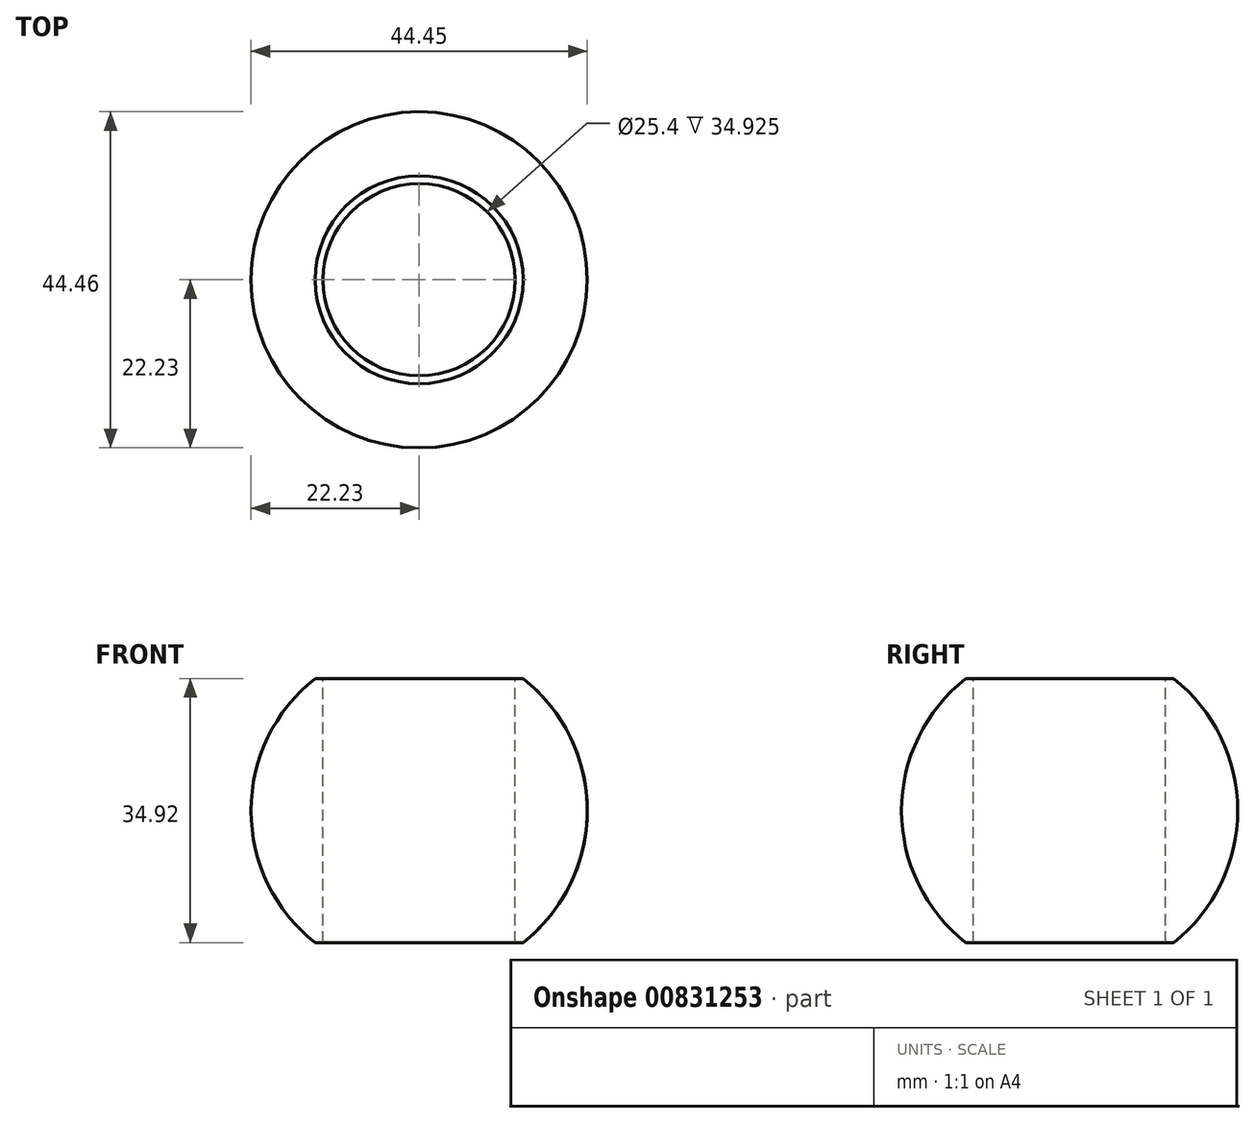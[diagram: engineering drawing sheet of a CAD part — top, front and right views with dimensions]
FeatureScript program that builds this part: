
annotation { "Feature Type Name" : "Feature", "Feature Type Description" : "" }
export const myFeature = defineFeature(function(context is Context, id is Id, definition is map)
    precondition{}
    {
        {
            var Q0;
            Q0=qCreatedBy(makeId("Front.planeOp"),FACE);
            var sketch = newSketch(context, id + "F0", { "sketchPlane" : qUnion([Q0])});
            skArc(sketch, "E0", {"start": v(-13.75, 17.46) * mm, "mid": v(-22.23, 0) * mm, "end": v(-13.75, -17.46) * mm});
            skLineSegment(sketch, "E1", {"start": v(0, 17.46) * mm, "end": v(0, -17.46) * mm, "construction": true});
            skLineSegment(sketch, "E2", {"start": v(-13.75, 17.46) * mm, "end": v(-12.7, 17.46) * mm});
            skLineSegment(sketch, "E3", {"start": v(-12.7, -17.46) * mm, "end": v(-13.75, -17.46) * mm});
            skPoint(sketch, "E4.orphan", {"position": v(0, 22.23) * mm});
            skLineSegment(sketch, "E5", {"start": v(-12.7, 17.46) * mm, "end": v(-12.7, -17.46) * mm});
            skSolve(sketch);
        }
        {
            var Q0;
            Q0 = qSketchRegion(id + "F0", true);
            var Q1;
            Q1=sQuery(id+"F0.wireOp",EDGE,"E1");
            revolve(context, id + "F1", {"surfaceOperationType" : NewSurfaceOperationType.NEW, "entities" : qUnion([Q0]), "axis" : qUnion([Q1]), "revolveType" : RevolveType.FULL});
        }
    });
